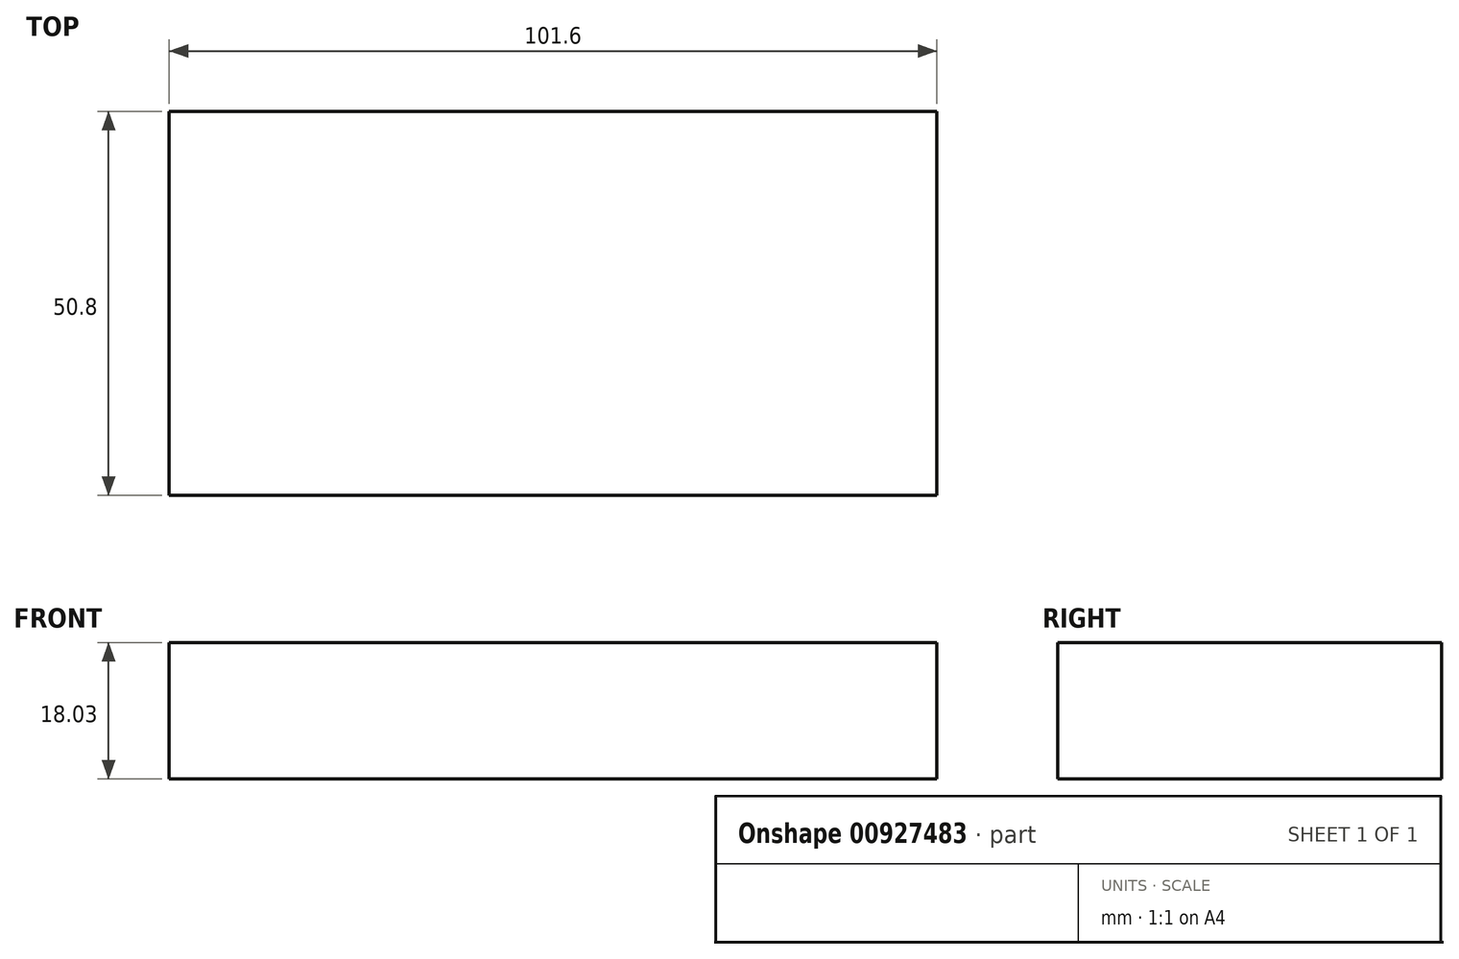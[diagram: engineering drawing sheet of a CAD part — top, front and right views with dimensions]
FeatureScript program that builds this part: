
annotation { "Feature Type Name" : "Feature", "Feature Type Description" : "" }
export const myFeature = defineFeature(function(context is Context, id is Id, definition is map)
    precondition{}
    {
        {
            var Q0;
            Q0=qCreatedBy(makeId("Top.planeOp"),FACE);
            var sketch = newSketch(context, id + "F0", { "sketchPlane" : qUnion([Q0])});
            skLineSegment(sketch, "E0.bottom", {"start": v(0, 0) * mm, "end": v(101.6, 0) * mm});
            skLineSegment(sketch, "E0.top", {"start": v(0, 50.8) * mm, "end": v(101.6, 50.8) * mm});
            skLineSegment(sketch, "E0.left", {"start": v(0, 0) * mm, "end": v(0, 50.8) * mm});
            skLineSegment(sketch, "E0.right", {"start": v(101.6, 0) * mm, "end": v(101.6, 50.8) * mm});
            skSolve(sketch);
        }
        {
            var Q0;
            Q0=makeQuery(id+"F0.imprint","IMPRINT",FACE,{"disambiguationData":[TD([[makeQuery(id+"F0.imprint","IMPRINT",EDGE,{"derivedFrom":sQuery(id+"F0.wireOp",EDGE,"E0.bottom")}),1.0]])]});
            extrude(context, id + "F1", {"entities" : qUnion([Q0]), "depth" : 18.03 * mm, "offsetDistance" : 25.4 * mm});
        }
    });
